# Revit family: HR3B
name_source: partatom
category: Generic Models
revit_build: Autodesk Revit LT 2017 (Build: 20160225_1515(x64)
units: mm (PartAtom-declared; Revit-internal decimal feet)

## family parameters
Always vertical = No
Can host rebar = No
Cut with Voids When Loaded = No
Part Type = Normal
Room Calculation Point = No
Round Connector Dimension = Use Diameter
Shared = No
Work Plane-Based = Yes

## types (1)
- NBS Standard Parameters
    BIMObjectName = Metpro_Metprolibrary_Conduitfittings_Metalcomponents_Steelaccessories
    Default Elevation = 1219 mm
    Description = HR3B  32 - 20mm Conduit Reducer
    DurationUnit = year
    Finish = Black
    Keynote = Compliant to LU Standard 1-085
    ManufacturerName = Metpro Ltd
    ManufacturerURL = www.metpro.co.uk
    Material = Mild Steel
    ModelReference = HR3B
    NBSDescription = Conduit Fittings
    NBSReference = 90-55-10/460
    NominalHeight = 23 mm
    NominalLength = 33 mm
    NominalWidth = 33 mm
    ProductInformation = www.metpro.co.uk/pdf/hr3g.pdf
    Shape = Circular
    Size = 32mm
    Uniclass2 = Pr_65_70_11_20
    Version = 1
    WarrantyDurationUnit = 1 year
    Weight = 0.092Kg

## geometry (parser evidence)
native form markers: Sweep x2
no freeform markers — native parametric forms only
